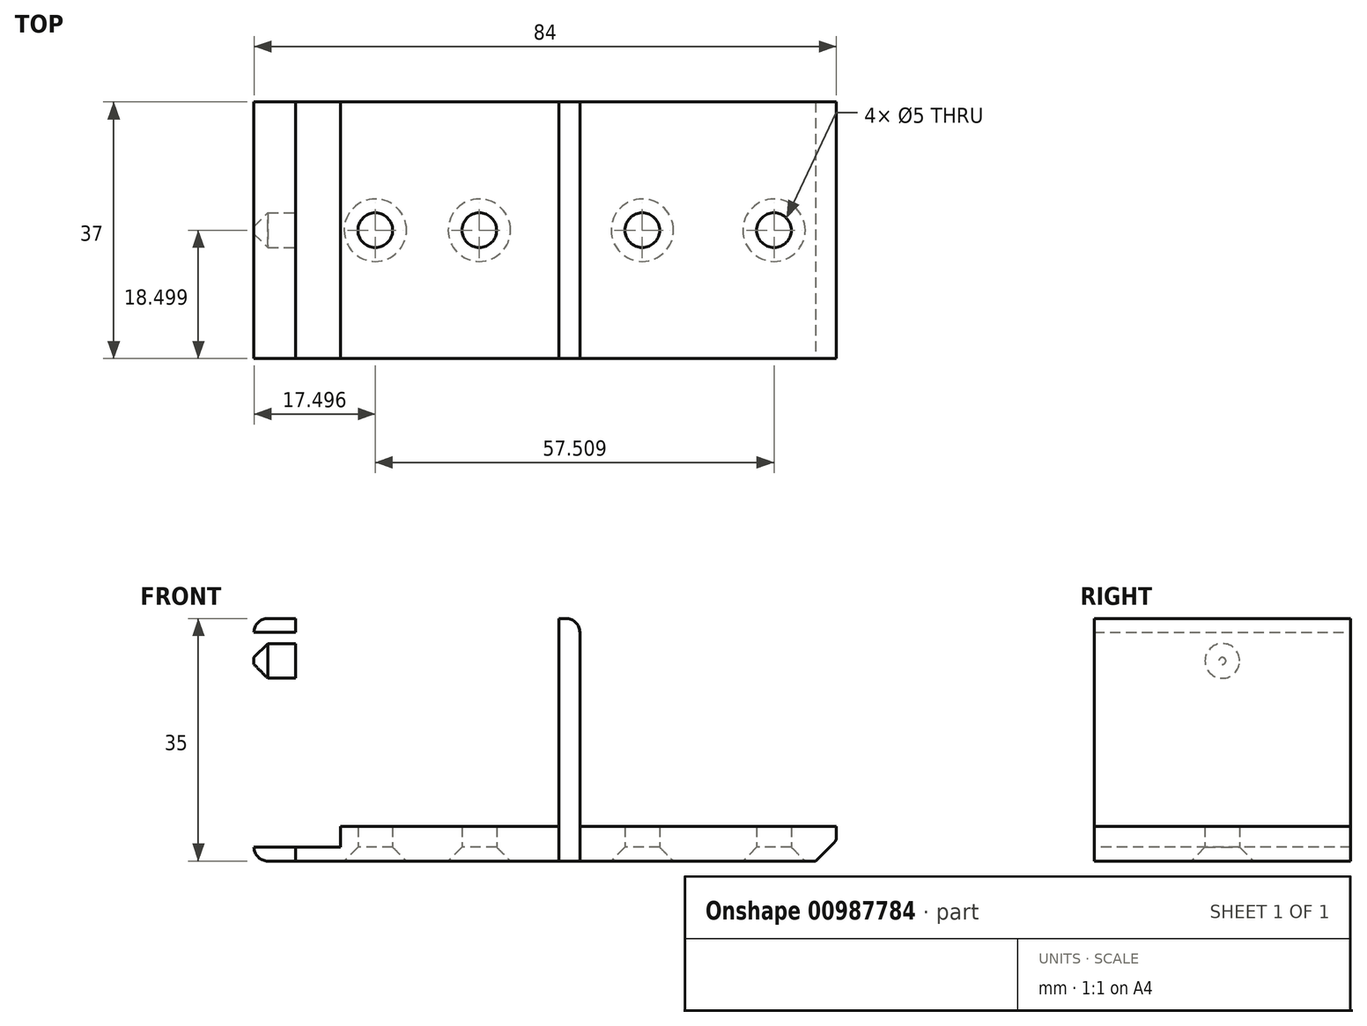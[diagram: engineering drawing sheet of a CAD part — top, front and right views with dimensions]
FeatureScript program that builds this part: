
annotation { "Feature Type Name" : "Feature", "Feature Type Description" : "" }
export const myFeature = defineFeature(function(context is Context, id is Id, definition is map)
    precondition{}
    {
        {
            var Q0;
            Q0=qCreatedBy(makeId("Top.planeOp"),FACE);
            var sketch = newSketch(context, id + "F0", { "sketchPlane" : qUnion([Q0])});
            skLineSegment(sketch, "E0.bottom", {"start": v(-89.34, 30.7) * mm, "end": v(-51.34, 30.7) * mm});
            skLineSegment(sketch, "E0.top", {"start": v(-89.34, -6.3) * mm, "end": v(-51.34, -6.3) * mm});
            skLineSegment(sketch, "E0.left", {"start": v(-89.34, 30.7) * mm, "end": v(-89.34, -6.3) * mm});
            skLineSegment(sketch, "E0.right", {"start": v(-51.34, 30.7) * mm, "end": v(-51.34, -6.3) * mm});
            skLineSegment(sketch, "E1.bottom", {"start": v(-51.34, 30.7) * mm, "end": v(-48.34, 30.7) * mm});
            skLineSegment(sketch, "E1.top", {"start": v(-51.34, -6.3) * mm, "end": v(-48.34, -6.3) * mm});
            skLineSegment(sketch, "E1.right", {"start": v(-48.34, 30.7) * mm, "end": v(-48.34, -6.3) * mm});
            skLineSegment(sketch, "E2.bottom", {"start": v(-89.34, 30.7) * mm, "end": v(-95.34, 30.7) * mm});
            skLineSegment(sketch, "E2.top", {"start": v(-89.34, -6.3) * mm, "end": v(-95.34, -6.3) * mm});
            skLineSegment(sketch, "E2.left", {"start": v(-89.34, 30.7) * mm, "end": v(-89.34, 12.2) * mm});
            skLineSegment(sketch, "E2.right", {"start": v(-95.34, 30.7) * mm, "end": v(-95.34, -6.3) * mm});
            skLineSegment(sketch, "E3.bottom", {"start": v(-48.34, 30.7) * mm, "end": v(-11.34, 30.7) * mm});
            skLineSegment(sketch, "E3.top", {"start": v(-48.34, -6.3) * mm, "end": v(-11.34, -6.3) * mm});
            skLineSegment(sketch, "E3.right", {"start": v(-11.34, 30.7) * mm, "end": v(-11.34, -6.3) * mm});
            skPoint(sketch, "E4", {"position": v(-20.34, 12.2) * mm});
            skPoint(sketch, "E4.positionSnap0", {"position": v(-11.34, 12.2) * mm});
            skPoint(sketch, "E5", {"position": v(-39.34, 12.2) * mm});
            skPoint(sketch, "E5.positionSnap0", {"position": v(-48.34, 12.2) * mm});
            skCircle(sketch, "E6", {"center": v(-39.34, 12.2) * mm, "radius": 2.5 * mm});
            skCircle(sketch, "E7", {"center": v(-20.34, 12.2) * mm, "radius": 2.5 * mm});
            skLineSegment(sketch, "E8", {"start": v(-89.34, 12.2) * mm, "end": v(-89.34, -6.3) * mm});
            skPoint(sketch, "E9.centerSnap0", {"position": v(-70.34, 30.7) * mm});
            skPoint(sketch, "E9.centerSnap1", {"position": v(-89.34, 21.46) * mm});
            skPoint(sketch, "E10.centerSnap0", {"position": v(-89.34, 2.96) * mm});
            skCircle(sketch, "E11", {"center": v(-62.84, 12.2) * mm, "radius": 2.5 * mm});
            skCircle(sketch, "E12", {"center": v(-77.84, 12.2) * mm, "radius": 2.5 * mm});
            skLineSegment(sketch, "E13", {"start": v(-77.84, 12.2) * mm, "end": v(-62.84, 12.2) * mm});
            skPoint(sketch, "E14", {"position": v(-70.34, 12.2) * mm});
            skSolve(sketch);
        }
        {
            var Q0;
            Q0=makeQuery(id+"F0.imprint","IMPRINT",FACE,{"disambiguationData":[TD([[makeQuery(id+"F0.imprint","IMPRINT",EDGE,{"derivedFrom":sQuery(id+"F0.wireOp",EDGE,"E2.bottom")}),1.0]])]});
            var Q1;
            Q1=makeQuery(id+"F0.imprint","IMPRINT",FACE,{"disambiguationData":[TD([[makeQuery(id+"F0.imprint","IMPRINT",EDGE,{"derivedFrom":sQuery(id+"F0.wireOp",EDGE,"E1.bottom")}),-1.0]])]});
            extrude(context, id + "F1", {"entities" : qUnion([Q0, Q1]), "depth" : 35 * mm, "offsetDistance" : 25 * mm});
        }
        {
            var Q0;
            Q0=makeQuery(id+"F0.imprint","IMPRINT",FACE,{"disambiguationData":[TD([[makeQuery(id+"F0.imprint","IMPRINT",EDGE,{"derivedFrom":sQuery(id+"F0.wireOp",EDGE,"E0.bottom")}),-1.0]])]});
            var Q1;
            Q1=makeQuery(id+"F0.imprint","IMPRINT",FACE,{"disambiguationData":[TD([[makeQuery(id+"F0.imprint","IMPRINT",EDGE,{"derivedFrom":sQuery(id+"F0.wireOp",EDGE,"E3.bottom")}),-1.0]])]});
            extrude(context, id + "F2", {"entities" : qUnion([Q0, Q1]), "depth" : 5 * mm, "offsetDistance" : 25 * mm});
        }
        {
            var Q0;
            Q0=makeQuery(id+"F2.opExtrude","CAP_EDGE",EDGE,{"disambiguationData":[OSD([sQuery(id+"F0.wireOp",EDGE,"E2.left"),sQuery(id+"F0.wireOp",EDGE,"E8")])],"isStart":false});
            var Q1;
            Q1=makeQuery(id+"F2.opExtrude","CAP_EDGE",EDGE,{"disambiguationData":[OSD([sQuery(id+"F0.wireOp",EDGE,"E0.right")])],"isStart":false});
            var Q2;
            Q2=makeQuery(id+"F1.opExtrude","CAP_EDGE",EDGE,{"disambiguationData":[OSD([sQuery(id+"F0.wireOp",EDGE,"E1.right")])],"isStart":false});
            fillet(context, id + "F3", {"entities" : qUnion([Q0, Q1, Q2]), "radius" : 2 * mm, "tangentPropagation" : true, "allowEdgeOverflow" : false});
        }
        {
            var Q0;
            Q0=makeQuery(id+"F2.opExtrude","CAP_EDGE",EDGE,{"disambiguationData":[OSD([sQuery(id+"F0.wireOp",EDGE,"E3.right")])],"isStart":true});
            chamfer(context, id + "F4", {"entities" : qUnion([Q0]), "width" : 3 * mm, "tangentPropagation" : true});
        }
        {
            var Q0;
            {var subQ0=sQuery(id+"F0.wireOp",EDGE,"E3.right");Q0=makeQuery(id+"F4.opChamfer","BLEND_EDGE",EDGE,{"blendedFrom":[makeQuery(id+"F2.opExtrude","CAP_EDGE",EDGE,{"disambiguationData":[OSD([subQ0])],"isStart":true}),makeQuery(id+"F2.opExtrude","SWEPT_FACE",FACE,{"disambiguationData":[OSD([subQ0])]})],"blendedInto":[makeQuery(id+"F2.opExtrude","SWEPT_FACE",FACE,{"disambiguationData":[OSD([subQ0])]})]});}
            fillet(context, id + "F5", {"entities" : qUnion([Q0]), "radius" : 1 * mm, "tangentPropagation" : true, "allowEdgeOverflow" : false});
        }
        {
            var Q0;
            Q0=makeQuery(id+"F2.opExtrude","CAP_EDGE",EDGE,{"disambiguationData":[OSD([sQuery(id+"F0.wireOp",EDGE,"8xzaLZzM-4nVU-31Vw-sQzU-5eVaGYc0uS2Y")])],"isStart":true});
            var Q1;
            Q1=makeQuery(id+"F2.opExtrude","CAP_EDGE",EDGE,{"disambiguationData":[OSD([sQuery(id+"F0.wireOp",EDGE,"E10")])],"isStart":true});
            var Q2;
            Q2=makeQuery(id+"F2.opExtrude","CAP_EDGE",EDGE,{"disambiguationData":[OSD([sQuery(id+"F0.wireOp",EDGE,"E9")])],"isStart":true});
            var Q3;
            Q3=makeQuery(id+"F2.opExtrude","CAP_EDGE",EDGE,{"disambiguationData":[OSD([sQuery(id+"F0.wireOp",EDGE,"E11")])],"isStart":true});
            var Q4;
            Q4=makeQuery(id+"F2.opExtrude","CAP_EDGE",EDGE,{"disambiguationData":[OSD([sQuery(id+"F0.wireOp",EDGE,"E6")])],"isStart":true});
            var Q5;
            Q5=makeQuery(id+"F2.opExtrude","CAP_EDGE",EDGE,{"disambiguationData":[OSD([sQuery(id+"F0.wireOp",EDGE,"E7")])],"isStart":true});
            var Q6;
            Q6=makeQuery(id+"F2.opExtrude","CAP_EDGE",EDGE,{"disambiguationData":[OSD([sQuery(id+"F0.wireOp",EDGE,"E12")])],"isStart":true});
            chamfer(context, id + "F6", {"entities" : qUnion([Q0, Q1, Q2, Q3, Q4, Q5, Q6]), "width" : 2 * mm, "tangentPropagation" : true});
        }
        {
            var Q0;
            Q0=makeQuery(id+"F1.opExtrude","CAP_EDGE",EDGE,{"disambiguationData":[OSD([sQuery(id+"F0.wireOp",EDGE,"E2.right")])],"isStart":false});
            var Q1;
            Q1=makeQuery(id+"F1.opExtrude","CAP_EDGE",EDGE,{"disambiguationData":[OSD([sQuery(id+"F0.wireOp",EDGE,"E2.right")])],"isStart":true});
            fillet(context, id + "F7", {"entities" : qUnion([Q0, Q1]), "radius" : 2 * mm, "tangentPropagation" : true, "allowEdgeOverflow" : false});
        }
        {
            var Q0;
            Q0=makeQuery(id+"F1.opExtrude","SWEPT_FACE",FACE,{"disambiguationData":[OSD([sQuery(id+"F0.wireOp",EDGE,"E2.right")])]});
            var sketch = newSketch(context, id + "F8", { "sketchPlane" : qUnion([Q0])});
            skLineSegment(sketch, "E15", {"start": v(-12.2, 33) * mm, "end": v(-12.2, 2) * mm});
            skCircle(sketch, "E16", {"center": v(-12.2, 28.87) * mm, "radius": 2.5 * mm});
            skSolve(sketch);
        }
        {
            var Q0;
            {var subQ0=sQuery(id+"F8.wireOp",EDGE,"E16");var subQ1=sQuery(id+"F8.wireOp",EDGE,"E15");var subQ2=makeQuery(id+"F8.imprint","INTERSECT",VERTEX,{"disambiguationData":[OD(0.0)],"derivedFrom":[subQ1,subQ0]});Q0=makeQuery(id+"F8.imprint","IMPRINT",FACE,{"disambiguationData":[TD([[makeQuery(id+"F8.imprint","IMPRINT",EDGE,{"disambiguationData":[TD([[subQ2,-1.0]])],"derivedFrom":subQ1}),1.0]])]});}
            var Q1;
            {var subQ0=sQuery(id+"F8.wireOp",EDGE,"E16");var subQ1=sQuery(id+"F8.wireOp",EDGE,"E15");var subQ2=makeQuery(id+"F8.imprint","INTERSECT",VERTEX,{"disambiguationData":[OD(0.0)],"derivedFrom":[subQ1,subQ0]});Q1=makeQuery(id+"F8.imprint","IMPRINT",FACE,{"disambiguationData":[TD([[makeQuery(id+"F8.imprint","IMPRINT",EDGE,{"disambiguationData":[TD([[subQ2,-1.0]])],"derivedFrom":subQ1}),-1.0]])]});}
            extrude(context, id + "F9", {"entities" : qUnion([Q0, Q1]), "operationType" : NewBodyOperationType.REMOVE, "endBound" : BoundingType.SYMMETRIC, "depth" : 25 * mm, "offsetDistance" : 25 * mm});
        }
        {
            var Q0;
            Q0=makeQuery(id+"F9.boolean.opBoolean","INTERSECT",EDGE,{"derivedFrom":[makeQuery(id+"F1.opExtrude","SWEPT_FACE",FACE,{"disambiguationData":[OSD([sQuery(id+"F0.wireOp",EDGE,"E2.right")])]}),makeQuery(id+"F9.opExtrude","SWEPT_FACE",FACE,{"disambiguationData":[OSD([sQuery(id+"F8.wireOp",EDGE,"E16")])]})]});
            chamfer(context, id + "F10", {"entities" : qUnion([Q0]), "width" : 2 * mm, "tangentPropagation" : true});
        }
    });
